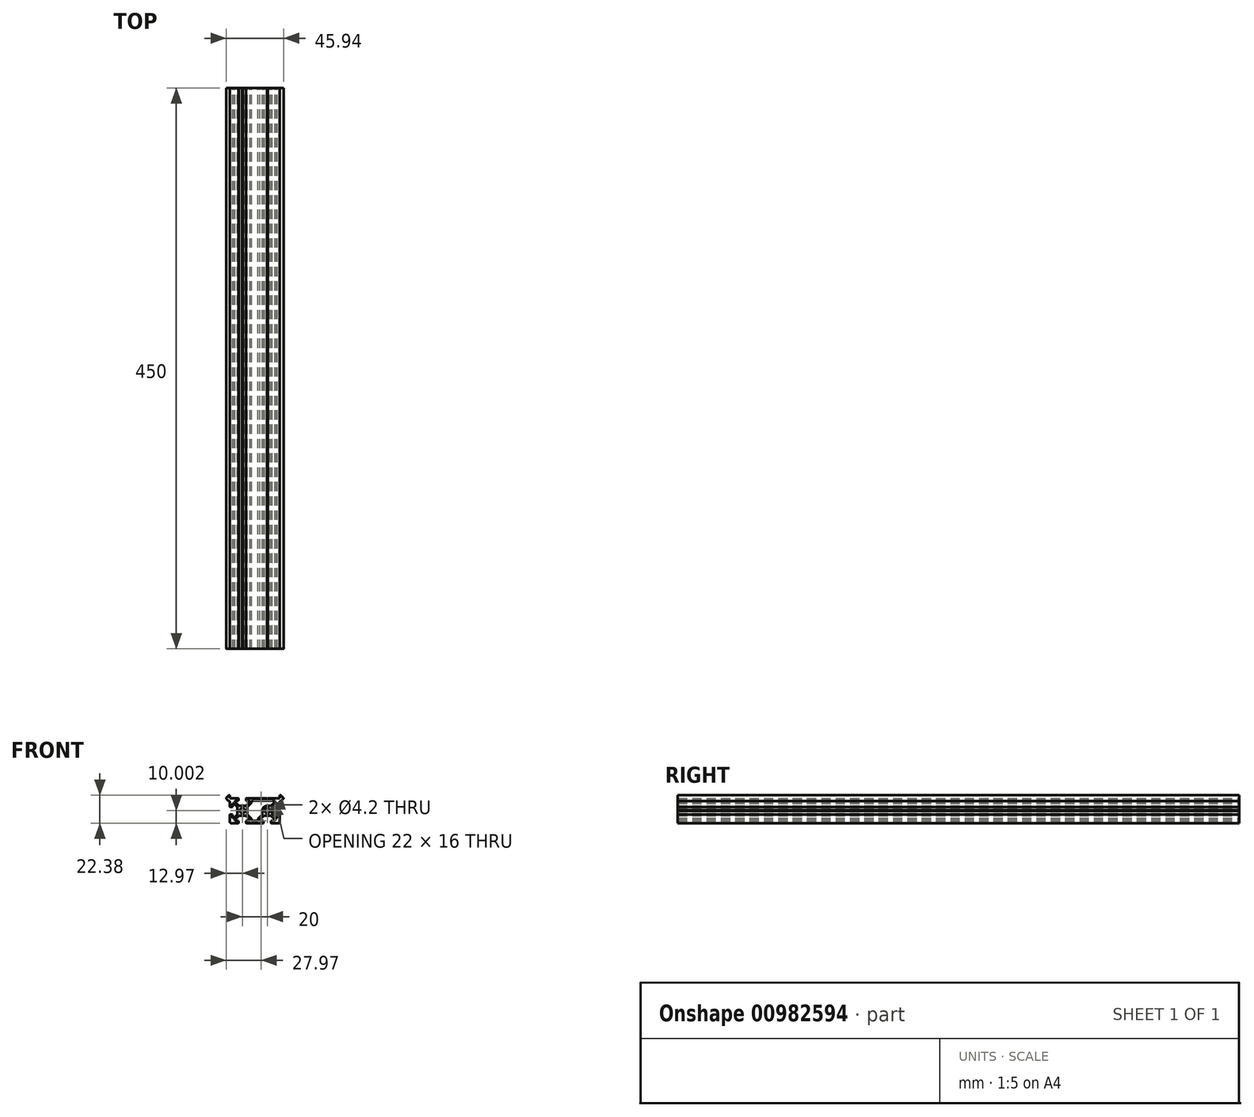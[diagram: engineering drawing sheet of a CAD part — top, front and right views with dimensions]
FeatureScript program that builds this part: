
annotation { "Feature Type Name" : "Feature", "Feature Type Description" : "" }
export const myFeature = defineFeature(function(context is Context, id is Id, definition is map)
    precondition{}
    {
        {
            assignVariable(context, id + "F0", {"name" : "Length", "anyValue" : 450 * mm});
        }
        {
            var Q0;
            Q0=qCreatedBy(makeId("Front.planeOp"),FACE);
            var sketch = newSketch(context, id + "F1", { "sketchPlane" : qUnion([Q0])});
            skArc(sketch, "E0", {"start": v(-20, 5.94) * mm, "mid": v(-20.15, 6.3) * mm, "end": v(-20.5, 6.44) * mm});
            skArc(sketch, "E1", {"start": v(20.5, 6.44) * mm, "mid": v(20.15, 6.3) * mm, "end": v(20, 5.94) * mm});
            skLineSegment(sketch, "E2", {"start": v(12.94, 2.81) * mm, "end": v(9.8, 2.81) * mm});
            skLineSegment(sketch, "E3", {"start": v(6, -1) * mm, "end": v(6, -4.13) * mm});
            skLineSegment(sketch, "E4", {"start": v(-2.5, 6.81) * mm, "end": v(16, 6.81) * mm});
            skLineSegment(sketch, "E5", {"start": v(6, -4.13) * mm, "end": v(2.5, -7.63) * mm});
            skLineSegment(sketch, "E6", {"start": v(2.5, -7.63) * mm, "end": v(2.5, -9.19) * mm});
            skLineSegment(sketch, "E7", {"start": v(2.5, -9.19) * mm, "end": v(-2.5, -9.19) * mm});
            skLineSegment(sketch, "E8", {"start": v(-2.5, -9.19) * mm, "end": v(-2.5, -7.63) * mm});
            skLineSegment(sketch, "E9", {"start": v(-2.5, -7.63) * mm, "end": v(-6, -4.13) * mm});
            skLineSegment(sketch, "E10", {"start": v(-6, -4.13) * mm, "end": v(-6, 1.75) * mm});
            skLineSegment(sketch, "E11", {"start": v(-6, 1.75) * mm, "end": v(-2.5, 5.25) * mm});
            skLineSegment(sketch, "E12", {"start": v(-2.5, 5.25) * mm, "end": v(-2.5, 6.81) * mm});
            skLineSegment(sketch, "E13", {"start": v(16, 6.81) * mm, "end": v(16, 5.87) * mm});
            skLineSegment(sketch, "E14", {"start": v(16, 5.87) * mm, "end": v(12.94, 2.81) * mm});
            skArc(sketch, "E15", {"start": v(9.8, 2.81) * mm, "mid": v(7.12, 1.7) * mm, "end": v(6, -1) * mm});
            skArc(sketch, "E16", {"start": v(12.1, -1.19) * mm, "mid": v(11.48, 0.3) * mm, "end": v(10, 0.91) * mm});
            skArc(sketch, "E17", {"start": v(10, -3.29) * mm, "mid": v(11.48, -2.67) * mm, "end": v(12.1, -1.19) * mm});
            skArc(sketch, "E18", {"start": v(7.9, -1.19) * mm, "mid": v(8.52, -2.67) * mm, "end": v(10, -3.29) * mm});
            skArc(sketch, "E19", {"start": v(10, 0.91) * mm, "mid": v(8.52, 0.3) * mm, "end": v(7.9, -1.19) * mm});
            skArc(sketch, "E20", {"start": v(-7.9, -1.19) * mm, "mid": v(-8.52, 0.3) * mm, "end": v(-10, 0.91) * mm});
            skArc(sketch, "E21", {"start": v(-10, -3.29) * mm, "mid": v(-8.52, -2.67) * mm, "end": v(-7.9, -1.19) * mm});
            skArc(sketch, "E22", {"start": v(-12.1, -1.19) * mm, "mid": v(-11.48, -2.67) * mm, "end": v(-10, -3.29) * mm});
            skArc(sketch, "E23", {"start": v(-10, 0.91) * mm, "mid": v(-11.48, 0.3) * mm, "end": v(-12.1, -1.19) * mm});
            skLineSegment(sketch, "E24", {"start": v(20.6, 11.19) * mm, "end": v(20, 11.19) * mm});
            skLineSegment(sketch, "E25", {"start": v(20, 11.19) * mm, "end": v(20, 8.81) * mm});
            skLineSegment(sketch, "E26", {"start": v(20, 8.81) * mm, "end": v(10.3, 8.81) * mm});
            skLineSegment(sketch, "E27", {"start": v(10, 8.51) * mm, "end": v(10.3, 8.81) * mm});
            skLineSegment(sketch, "E28", {"start": v(9.7, 8.81) * mm, "end": v(10, 8.51) * mm});
            skLineSegment(sketch, "E29", {"start": v(9.7, 8.81) * mm, "end": v(-6.7, 8.81) * mm});
            skArc(sketch, "E30", {"start": v(-6.7, 8.81) * mm, "mid": v(-6.91, 8.72) * mm, "end": v(-7, 8.51) * mm});
            skLineSegment(sketch, "E31", {"start": v(-7, 8.51) * mm, "end": v(-7, 6.81) * mm});
            skLineSegment(sketch, "E32", {"start": v(-7, 6.81) * mm, "end": v(-4, 6.81) * mm});
            skLineSegment(sketch, "E33", {"start": v(-4, 6.81) * mm, "end": v(-4, 5.87) * mm});
            skLineSegment(sketch, "E34", {"start": v(-4, 5.87) * mm, "end": v(-7.06, 2.81) * mm});
            skLineSegment(sketch, "E35", {"start": v(-7.06, 2.81) * mm, "end": v(-9.7, 2.81) * mm});
            skLineSegment(sketch, "E36", {"start": v(-9.7, 2.81) * mm, "end": v(-10, 2.51) * mm});
            skLineSegment(sketch, "E37", {"start": v(-10, 2.51) * mm, "end": v(-10.3, 2.81) * mm});
            skLineSegment(sketch, "E38", {"start": v(-10.3, 2.81) * mm, "end": v(-12.94, 2.81) * mm});
            skLineSegment(sketch, "E39", {"start": v(-12.94, 2.81) * mm, "end": v(-16, 5.87) * mm});
            skLineSegment(sketch, "E40", {"start": v(-16, 5.87) * mm, "end": v(-16, 6.81) * mm});
            skLineSegment(sketch, "E41", {"start": v(-16, 6.81) * mm, "end": v(-13, 6.81) * mm});
            skLineSegment(sketch, "E42", {"start": v(-13, 6.81) * mm, "end": v(-13, 8.51) * mm});
            skArc(sketch, "E43", {"start": v(-13, 8.51) * mm, "mid": v(-13.09, 8.72) * mm, "end": v(-13.3, 8.81) * mm});
            skLineSegment(sketch, "E44", {"start": v(-13.3, 8.81) * mm, "end": v(-20, 8.81) * mm});
            skLineSegment(sketch, "E45", {"start": v(-20, 11.19) * mm, "end": v(-20, 8.81) * mm});
            skLineSegment(sketch, "E46", {"start": v(-20.6, 11.19) * mm, "end": v(-20, 11.19) * mm});
            skArc(sketch, "E47", {"start": v(-20.6, 11.19) * mm, "mid": v(-20.78, 11.15) * mm, "end": v(-20.95, 11.04) * mm});
            skLineSegment(sketch, "E48", {"start": v(-22.82, 9.17) * mm, "end": v(-20.95, 11.04) * mm});
            skArc(sketch, "E49", {"start": v(-22.82, 9.17) * mm, "mid": v(-22.97, 8.81) * mm, "end": v(-22.82, 8.46) * mm});
            skLineSegment(sketch, "E50", {"start": v(-20.95, 6.58) * mm, "end": v(-22.82, 8.46) * mm});
            skArc(sketch, "E51", {"start": v(-20.95, 6.58) * mm, "mid": v(-20.78, 6.48) * mm, "end": v(-20.6, 6.44) * mm});
            skLineSegment(sketch, "E52", {"start": v(-20.5, 6.44) * mm, "end": v(-20.6, 6.44) * mm});
            skLineSegment(sketch, "E53", {"start": v(-20, 5.94) * mm, "end": v(-20, 2.11) * mm});
            skArc(sketch, "E54", {"start": v(-20, 2.11) * mm, "mid": v(-19.91, 1.9) * mm, "end": v(-19.7, 1.81) * mm});
            skLineSegment(sketch, "E55", {"start": v(-19.7, 1.81) * mm, "end": v(-18, 1.81) * mm});
            skLineSegment(sketch, "E56", {"start": v(-18, 1.81) * mm, "end": v(-18, 4.81) * mm});
            skLineSegment(sketch, "E57", {"start": v(-18, 4.81) * mm, "end": v(-17.06, 4.81) * mm});
            skLineSegment(sketch, "E58", {"start": v(-17.06, 4.81) * mm, "end": v(-14, 1.75) * mm});
            skLineSegment(sketch, "E59", {"start": v(-14, 1.75) * mm, "end": v(-14, -0.89) * mm});
            skLineSegment(sketch, "E60", {"start": v(-14, -0.89) * mm, "end": v(-13.7, -1.19) * mm});
            skLineSegment(sketch, "E61", {"start": v(-13.7, -1.19) * mm, "end": v(-14, -1.49) * mm});
            skLineSegment(sketch, "E62", {"start": v(-14, -1.49) * mm, "end": v(-14, -4.13) * mm});
            skLineSegment(sketch, "E63", {"start": v(-14, -4.13) * mm, "end": v(-17.06, -7.19) * mm});
            skLineSegment(sketch, "E64", {"start": v(-17.06, -7.19) * mm, "end": v(-18, -7.19) * mm});
            skLineSegment(sketch, "E65", {"start": v(-18, -7.19) * mm, "end": v(-18, -4.19) * mm});
            skLineSegment(sketch, "E66", {"start": v(-18, -4.19) * mm, "end": v(-19.7, -4.19) * mm});
            skArc(sketch, "E67", {"start": v(-19.7, -4.19) * mm, "mid": v(-19.91, -4.28) * mm, "end": v(-20, -4.49) * mm});
            skLineSegment(sketch, "E68", {"start": v(-20, -4.49) * mm, "end": v(-20, -10.19) * mm});
            skArc(sketch, "E69", {"start": v(-20, -10.19) * mm, "mid": v(-19.7, -10.9) * mm, "end": v(-19, -11.19) * mm});
            skLineSegment(sketch, "E70", {"start": v(-19, -11.19) * mm, "end": v(-13.3, -11.19) * mm});
            skArc(sketch, "E71", {"start": v(-13.3, -11.19) * mm, "mid": v(-13.09, -11.1) * mm, "end": v(-13, -10.89) * mm});
            skLineSegment(sketch, "E72", {"start": v(-13, -10.89) * mm, "end": v(-13, -9.19) * mm});
            skLineSegment(sketch, "E73", {"start": v(-13, -9.19) * mm, "end": v(-16, -9.19) * mm});
            skLineSegment(sketch, "E74", {"start": v(-16, -9.19) * mm, "end": v(-16, -8.25) * mm});
            skLineSegment(sketch, "E75", {"start": v(-16, -8.25) * mm, "end": v(-12.94, -5.19) * mm});
            skLineSegment(sketch, "E76", {"start": v(-12.94, -5.19) * mm, "end": v(-10.3, -5.19) * mm});
            skLineSegment(sketch, "E77", {"start": v(-10.3, -5.19) * mm, "end": v(-10, -4.89) * mm});
            skLineSegment(sketch, "E78", {"start": v(-10, -4.89) * mm, "end": v(-9.7, -5.19) * mm});
            skLineSegment(sketch, "E79", {"start": v(-9.7, -5.19) * mm, "end": v(-7.06, -5.19) * mm});
            skLineSegment(sketch, "E80", {"start": v(-7.06, -5.19) * mm, "end": v(-4, -8.25) * mm});
            skLineSegment(sketch, "E81", {"start": v(-4, -8.25) * mm, "end": v(-4, -9.19) * mm});
            skLineSegment(sketch, "E82", {"start": v(-4, -9.19) * mm, "end": v(-7, -9.19) * mm});
            skLineSegment(sketch, "E83", {"start": v(-7, -9.19) * mm, "end": v(-7, -10.89) * mm});
            skArc(sketch, "E84", {"start": v(-7, -10.89) * mm, "mid": v(-6.91, -11.1) * mm, "end": v(-6.7, -11.19) * mm});
            skLineSegment(sketch, "E85", {"start": v(-6.7, -11.19) * mm, "end": v(6.7, -11.19) * mm});
            skArc(sketch, "E86", {"start": v(6.7, -11.19) * mm, "mid": v(6.91, -11.1) * mm, "end": v(7, -10.89) * mm});
            skLineSegment(sketch, "E87", {"start": v(7, -10.89) * mm, "end": v(7, -9.19) * mm});
            skLineSegment(sketch, "E88", {"start": v(7, -9.19) * mm, "end": v(4, -9.19) * mm});
            skLineSegment(sketch, "E89", {"start": v(4, -9.19) * mm, "end": v(4, -8.25) * mm});
            skLineSegment(sketch, "E90", {"start": v(4, -8.25) * mm, "end": v(7.06, -5.19) * mm});
            skLineSegment(sketch, "E91", {"start": v(7.06, -5.19) * mm, "end": v(9.7, -5.19) * mm});
            skLineSegment(sketch, "E92", {"start": v(9.7, -5.19) * mm, "end": v(10, -4.89) * mm});
            skLineSegment(sketch, "E93", {"start": v(10, -4.89) * mm, "end": v(10.3, -5.19) * mm});
            skLineSegment(sketch, "E94", {"start": v(10.3, -5.19) * mm, "end": v(12.94, -5.19) * mm});
            skLineSegment(sketch, "E95", {"start": v(12.94, -5.19) * mm, "end": v(16, -8.25) * mm});
            skLineSegment(sketch, "E96", {"start": v(16, -8.25) * mm, "end": v(16, -9.19) * mm});
            skLineSegment(sketch, "E97", {"start": v(16, -9.19) * mm, "end": v(13, -9.19) * mm});
            skLineSegment(sketch, "E98", {"start": v(13, -9.19) * mm, "end": v(13, -10.89) * mm});
            skArc(sketch, "E99", {"start": v(13, -10.89) * mm, "mid": v(13.09, -11.1) * mm, "end": v(13.3, -11.19) * mm});
            skLineSegment(sketch, "E100", {"start": v(13.3, -11.19) * mm, "end": v(19, -11.19) * mm});
            skArc(sketch, "E101", {"start": v(19, -11.19) * mm, "mid": v(19.7, -10.9) * mm, "end": v(20, -10.19) * mm});
            skLineSegment(sketch, "E102", {"start": v(20, -10.19) * mm, "end": v(20, -4.49) * mm});
            skArc(sketch, "E103", {"start": v(20, -4.49) * mm, "mid": v(19.91, -4.28) * mm, "end": v(19.7, -4.19) * mm});
            skLineSegment(sketch, "E104", {"start": v(19.7, -4.19) * mm, "end": v(18, -4.19) * mm});
            skLineSegment(sketch, "E105", {"start": v(18, -4.19) * mm, "end": v(18, -7.19) * mm});
            skLineSegment(sketch, "E106", {"start": v(18, -7.19) * mm, "end": v(17.06, -7.19) * mm});
            skLineSegment(sketch, "E107", {"start": v(17.06, -7.19) * mm, "end": v(14, -4.13) * mm});
            skLineSegment(sketch, "E108", {"start": v(14, -4.13) * mm, "end": v(14, -1.49) * mm});
            skLineSegment(sketch, "E109", {"start": v(14, -1.49) * mm, "end": v(13.7, -1.19) * mm});
            skLineSegment(sketch, "E110", {"start": v(13.7, -1.19) * mm, "end": v(14, -0.89) * mm});
            skLineSegment(sketch, "E111", {"start": v(14, -0.89) * mm, "end": v(14, 1.75) * mm});
            skLineSegment(sketch, "E112", {"start": v(14, 1.75) * mm, "end": v(17.06, 4.81) * mm});
            skLineSegment(sketch, "E113", {"start": v(17.06, 4.81) * mm, "end": v(18, 4.81) * mm});
            skLineSegment(sketch, "E114", {"start": v(18, 4.81) * mm, "end": v(18, 1.81) * mm});
            skLineSegment(sketch, "E115", {"start": v(18, 1.81) * mm, "end": v(19.7, 1.81) * mm});
            skArc(sketch, "E116", {"start": v(19.7, 1.81) * mm, "mid": v(19.91, 1.9) * mm, "end": v(20, 2.11) * mm});
            skLineSegment(sketch, "E117", {"start": v(20, 2.11) * mm, "end": v(20, 5.94) * mm});
            skLineSegment(sketch, "E118", {"start": v(20.5, 6.44) * mm, "end": v(20.6, 6.44) * mm});
            skArc(sketch, "E119", {"start": v(20.95, 11.04) * mm, "mid": v(20.78, 11.15) * mm, "end": v(20.6, 11.19) * mm});
            skLineSegment(sketch, "E120", {"start": v(22.82, 9.17) * mm, "end": v(20.95, 11.04) * mm});
            skArc(sketch, "E121", {"start": v(22.82, 8.46) * mm, "mid": v(22.97, 8.81) * mm, "end": v(22.82, 9.17) * mm});
            skLineSegment(sketch, "E122", {"start": v(20.95, 6.58) * mm, "end": v(22.82, 8.46) * mm});
            skArc(sketch, "E123", {"start": v(20.6, 6.44) * mm, "mid": v(20.78, 6.48) * mm, "end": v(20.95, 6.58) * mm});
            skSolve(sketch);
        }
        {
            var Q0;
            Q0=makeQuery(id+"F1.imprint","IMPRINT",FACE,{"disambiguationData":[TD([[makeQuery(id+"F1.imprint","IMPRINT",EDGE,{"derivedFrom":sQuery(id+"F1.wireOp",EDGE,"E0")}),-1.0]])]});
            extrude(context, id + "F2", {"entities" : qUnion([Q0]), "depth" : getVariable(context, 'Length'), "offsetDistance" : 25 * mm});
        }
    });
